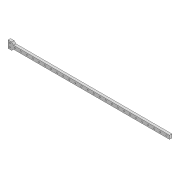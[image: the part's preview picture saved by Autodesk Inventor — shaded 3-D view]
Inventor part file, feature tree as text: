
AUTODESK INVENTOR PART (.ipt)
format: ipt  version: 2022 (Build 260153000, 153)  size: 134,656 bytes
history: native  units: mm
features: extrude x2, sketch x2, pattern_linear x1, chamfer x1
ambient origin geometry x8: Origin, YZ Plane, XZ Plane, XY Plane, X Axis, Y Axis, Z Axis, Center Point
bodies: Solid1 (feature_tree)
feature tree (6):
  extrude  "Extrusion1"  Depth=2.1mm
  extrude  "Extrusion2"  Depth=3.0mm
  pattern_linear  "Rectangular Pattern1"  Spacing1=3.0mm  [1 undecoded]
  chamfer  "Chamfer1"  Distance=12.0mm
  sketch  "Sketch1"  dims[d0=2.1mm d1=2.1mm]
  sketch  "Sketch2"  dims[d2=5.9mm d3=3.0mm d4=3.0mm d5=12.0mm d6=3.05mm d7=260.0mm d8=4.0mm d9=0.0mm d10=2.0mm d11=5.0mm d12=10.0mm d13=0.0mm d14=260.0mm d16=10.0mm d17=3.0mm d18=2.0mm d19=45.0deg]
note: 1 required parameter value undecoded (feature->parameter linkage not recoverable at this tier; creation-order binding heuristic only, values carry confidence <= 0.55)
